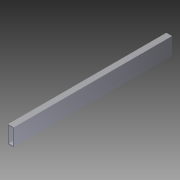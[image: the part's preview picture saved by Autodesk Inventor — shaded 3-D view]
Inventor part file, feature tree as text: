
AUTODESK INVENTOR PART (.ipt)
format: ipt  version: 2012 (Build 160160000, 160)  size: 74,752 bytes
history: native  units: in
note: dims shown in document units (in); Inventor stores cm internally (conversion verified against a paired STEP export)
features: extrude x1, sketch x1
ambient origin geometry x8: Origin, YZ Plane, XZ Plane, XY Plane, X Axis, Y Axis, Z Axis, Center Point
bodies: Solid1 (feature_tree)
feature tree (2):
  extrude  "Extrusion1"  Depth=1.0in
  sketch  "Sketch1"  dims[d0=3.0in d1=1.0in d2=0.125in d3=0.125in d4=0.125in d5=0.125in d6=27.75in d7=0.0in]
